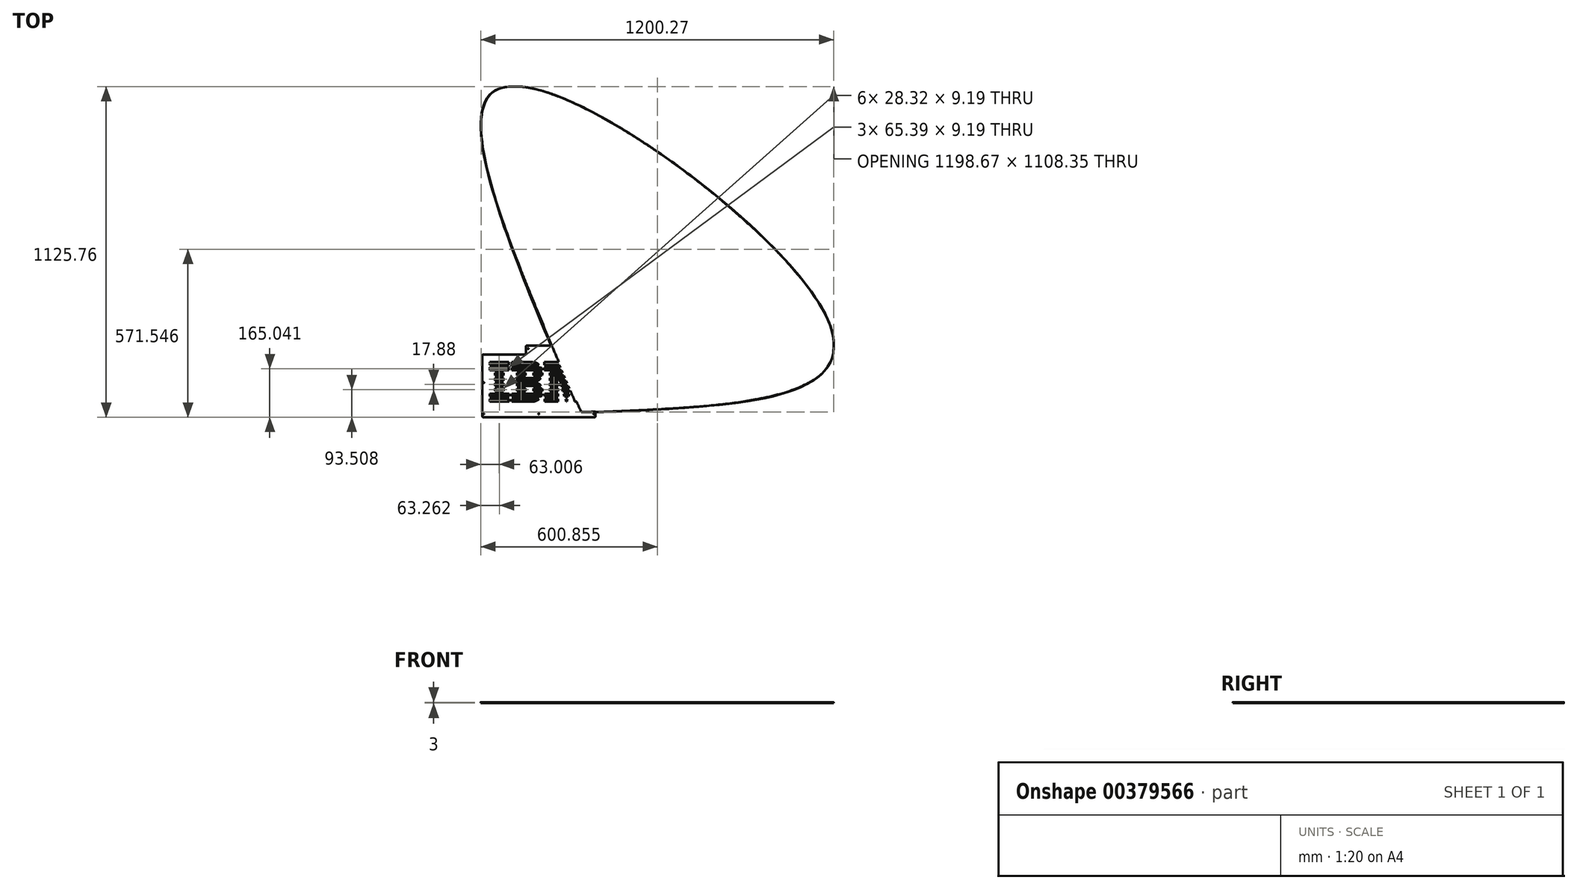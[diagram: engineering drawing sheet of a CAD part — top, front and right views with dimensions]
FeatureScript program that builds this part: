
annotation { "Feature Type Name" : "Feature", "Feature Type Description" : "" }
export const myFeature = defineFeature(function(context is Context, id is Id, definition is map)
    precondition{}
    {
        {
            var Q0;
            Q0=qCreatedBy(makeId("Top.planeOp"),FACE);
            var sketch = newSketch(context, id + "F0", { "sketchPlane" : qUnion([Q0])});
            skLineSegment(sketch, "E0.bottom", {"start": v(-188.4, -124.67) * mm, "end": v(188.48, -124.67) * mm});
            skLineSegment(sketch, "E0.left", {"start": v(-192.36, -120.71) * mm, "end": v(-192.36, 85.08) * mm});
            skPoint(sketch, "E1.visualSharp", {"position": v(-192.36, -124.67) * mm});
            skArc(sketch, "E1.filletArc", {"start": v(-192.36, -120.71) * mm, "mid": v(-191.2, -123.51) * mm, "end": v(-188.4, -124.67) * mm});
            skFitSpline(sketch, "E2", {"points": [v(151.72, -93.23) * mm, v(1000, 151.27) * mm, v(-92.62, 1000) * mm, v(150.35, -91.7) * mm]});
            skFitSpline(sketch, "E3", {"points": [v(147.19, -90.26) * mm, v(1000, 146.42) * mm, v(-90.07, 1000) * mm, v(145.01, -90.03) * mm]});
            skFitSpline(sketch, "E4", {"points": [v(149.93, -91.42) * mm, v(1000, 149.1) * mm, v(-90.88, 1000) * mm, v(148.23, -90.51) * mm]});
            skLineSegment(sketch, "E5", {"start": v(140.1, -108.72) * mm, "end": v(141.58, -106.96) * mm});
            skFitSpline(sketch, "E6", {"points": [v(139.4, -105.36) * mm, v(1000, 138.97) * mm, v(-106.35, 1000) * mm, v(138.57, -107.27) * mm]});
            skFitSpline(sketch, "E7", {"points": [v(141.58, -106.96) * mm, v(1000, 142.67) * mm, v(-105.67, 1000) * mm, v(143.1, -105.2) * mm]});
            skFitSpline(sketch, "E8", {"points": [v(144.18, -90.15) * mm, v(1000, 142.33) * mm, v(-90.45, 1000) * mm, v(140.47, -91.55) * mm]});
            skFitSpline(sketch, "E9", {"points": [v(144.37, -105.53) * mm, v(1000, 144.43) * mm, v(-105.53, 1000) * mm, v(144.48, -105.58) * mm]});
            skFitSpline(sketch, "E10", {"points": [v(144.87, -107.32) * mm, v(1000, 145.05) * mm, v(-108.17, 1000) * mm, v(145.23, -109) * mm]});
            skLineSegment(sketch, "E11", {"start": v(145.27, -109.17) * mm, "end": v(145.34, -109.48) * mm});
            skLineSegment(sketch, "E12", {"start": v(145.34, -109.48) * mm, "end": v(145.8, -109.46) * mm});
            skFitSpline(sketch, "E13", {"points": [v(139, -108.05) * mm, v(1000, 139.33) * mm, v(-108.27, 1000) * mm, v(139.7, -108.5) * mm]});
            skFitSpline(sketch, "E14", {"points": [v(145.8, -109.46) * mm, v(1000, 146.07) * mm, v(-109.46, 1000) * mm, v(146.5, -109.44) * mm]});
            skFitSpline(sketch, "E15", {"points": [v(139.4, -93) * mm, v(1000, 137.05) * mm, v(-96.17, 1000) * mm, v(137.32, -100.36) * mm]});
            skFitSpline(sketch, "E16", {"points": [v(140.2, -103.51) * mm, v(1000, 140.2) * mm, v(-103.54, 1000) * mm, v(139.83, -104.37) * mm]});
            skLineSegment(sketch, "E17", {"start": v(138.52, -107.41) * mm, "end": v(138.42, -107.66) * mm});
            skLineSegment(sketch, "E18", {"start": v(138.42, -107.66) * mm, "end": v(139, -108.05) * mm});
            skFitSpline(sketch, "E19", {"points": [v(143.16, -105.23) * mm, v(1000, 143.31) * mm, v(-105.29, 1000) * mm, v(144.27, -105.53) * mm]});
            skFitSpline(sketch, "E20", {"points": [v(144.5, -105.65) * mm, v(1000, 144.52) * mm, v(-105.72, 1000) * mm, v(144.68, -106.47) * mm]});
            skFitSpline(sketch, "E21", {"points": [v(140.05, -103.26) * mm, v(1000, 140.15) * mm, v(-103.37, 1000) * mm, v(140.22, -103.48) * mm]});
            skLineSegment(sketch, "E22", {"start": v(139.84, -108.58) * mm, "end": v(140.1, -108.72) * mm});
            skFitSpline(sketch, "E23", {"points": [v(147.38, -108.76) * mm, v(1000, 147.43) * mm, v(-108.06, 1000) * mm, v(147.64, -105.39) * mm]});
            skFitSpline(sketch, "E24", {"points": [v(146.8, -109.42) * mm, v(1000, 147.37) * mm, v(-109.38, 1000) * mm, v(147.33, -109.43) * mm]});
            skFitSpline(sketch, "E25", {"points": [v(149.02, -104.86) * mm, v(1000, 149.05) * mm, v(-104.86, 1000) * mm, v(149.6, -105.34) * mm]});
            skFitSpline(sketch, "E26", {"points": [v(147.65, -105.38) * mm, v(147.95, -105.27) * mm, v(148.3, -105.12) * mm]});
            skFitSpline(sketch, "E27", {"points": [v(148.3, -105.12) * mm, v(1000, 148.66) * mm, v(-104.98, 1000) * mm, v(148.98, -104.86) * mm]});
            skFitSpline(sketch, "E28", {"points": [v(150.24, -105.93) * mm, v(1000, 150.89) * mm, v(-106.5, 1000) * mm, v(151.63, -107.18) * mm]});
            skFitSpline(sketch, "E29", {"points": [v(151.89, -107.42) * mm, v(1000, 152.15) * mm, v(-107.65, 1000) * mm, v(152.4, -107.85) * mm]});
            skFitSpline(sketch, "E30", {"points": [v(152.44, -107.85) * mm, v(1000, 152.5) * mm, v(-107.85, 1000) * mm, v(153.4, -107.13) * mm]});
            skLineSegment(sketch, "E31", {"start": v(153.94, -106.64) * mm, "end": v(153.76, -106.32) * mm});
            skFitSpline(sketch, "E32", {"points": [v(153.76, -106.32) * mm, v(1000, 153.66) * mm, v(-106.14, 1000) * mm, v(153.14, -105.28) * mm]});
            skFitSpline(sketch, "E33", {"points": [v(152.62, -104.4) * mm, v(1000, 152.1) * mm, v(-103.53, 1000) * mm, v(151.66, -102.8) * mm]});
            skLineSegment(sketch, "E34", {"start": v(153.78, -106.8) * mm, "end": v(153.94, -106.64) * mm});
            skFitSpline(sketch, "E35", {"points": [v(151.66, -102.79) * mm, v(1000, 151.66) * mm, v(-102.77, 1000) * mm, v(151.8, -102.55) * mm]});
            skLineSegment(sketch, "E36", {"start": v(153.26, -98.4) * mm, "end": v(151.6, -98.41) * mm});
            skLineSegment(sketch, "E37", {"start": v(153.22, -98.72) * mm, "end": v(153.26, -98.4) * mm});
            skLineSegment(sketch, "E38", {"start": v(149.92, -98.43) * mm, "end": v(149.88, -98.78) * mm});
            skLineSegment(sketch, "E39", {"start": v(151.6, -98.41) * mm, "end": v(149.92, -98.43) * mm});
            skFitSpline(sketch, "E40", {"points": [v(149.88, -98.78) * mm, v(1000, 149.81) * mm, v(-99.41, 1000) * mm, v(149.5, -100.18) * mm]});
            skFitSpline(sketch, "E41", {"points": [v(149.07, -100.71) * mm, v(1000, 148.78) * mm, v(-101.08, 1000) * mm, v(148.06, -101.66) * mm]});
            skFitSpline(sketch, "E42", {"points": [v(151.96, -102.3) * mm, v(1000, 152.67) * mm, v(-101.24, 1000) * mm, v(153.1, -99.98) * mm]});
            skFitSpline(sketch, "E43", {"points": [v(142.86, -101.31) * mm, v(1000, 142.54) * mm, v(-101, 1000) * mm, v(142.5, -100.92) * mm]});
            skFitSpline(sketch, "E44", {"points": [v(145.1, -102.44) * mm, v(1000, 144.17) * mm, v(-102.32, 1000) * mm, v(143.57, -102.02) * mm]});
            skFitSpline(sketch, "E45", {"points": [v(144.2, -99.88) * mm, v(1000, 148.92) * mm, v(-97.14, 1000) * mm, v(152.68, -94.92) * mm]});
            skFitSpline(sketch, "E46", {"points": [v(142.56, -100.86) * mm, v(1000, 142.6) * mm, v(-100.82, 1000) * mm, v(143.34, -100.38) * mm]});
            skFitSpline(sketch, "E47", {"points": [v(152.7, -94.87) * mm, v(1000, 152.73) * mm, v(-94.79, 1000) * mm, v(152.12, -93.76) * mm]});
            skFitSpline(sketch, "E48", {"points": [v(147.58, -101.9) * mm, v(1000, 146.72) * mm, v(-102.35, 1000) * mm, v(145.85, -102.53) * mm]});
            skLineSegment(sketch, "E49", {"start": v(-44.4, 115.08) * mm, "end": v(-44.4, 111.04) * mm});
            skLineSegment(sketch, "E50.trimOffspring", {"start": v(-40.43, 119.04) * mm, "end": v(188.48, 119.04) * mm});
            skPoint(sketch, "E51.visualSharp", {"position": v(-44.4, 119.04) * mm});
            skArc(sketch, "E51.filletArc", {"start": v(-40.43, 119.04) * mm, "mid": v(-43.23, 117.88) * mm, "end": v(-44.4, 115.08) * mm});
            skLineSegment(sketch, "E52", {"start": v(192.44, 115.08) * mm, "end": v(192.44, -120.71) * mm});
            skPoint(sketch, "E53.visualSharp", {"position": v(192.44, 119.04) * mm});
            skArc(sketch, "E53.filletArc", {"start": v(192.44, 115.08) * mm, "mid": v(191.28, 117.88) * mm, "end": v(188.48, 119.04) * mm});
            skPoint(sketch, "E54.visualSharp", {"position": v(192.44, -124.67) * mm});
            skArc(sketch, "E54.filletArc", {"start": v(188.48, -124.67) * mm, "mid": v(191.28, -123.51) * mm, "end": v(192.44, -120.71) * mm});
            skLineSegment(sketch, "E55", {"start": v(-188.4, 89.04) * mm, "end": v(-44.4, 89.04) * mm});
            skLineSegment(sketch, "E56", {"start": v(-44.4, 89.04) * mm, "end": v(-44.4, 111.04) * mm});
            skPoint(sketch, "E57.visualSharp", {"position": v(-192.36, 89.04) * mm});
            skArc(sketch, "E57.filletArc", {"start": v(-188.4, 89.04) * mm, "mid": v(-191.2, 87.88) * mm, "end": v(-192.36, 85.08) * mm});
            skLineSegment(sketch, "E58", {"start": v(51.66, -17.88) * mm, "end": v(65.82, -17.88) * mm});
            skLineSegment(sketch, "E59", {"start": v(65.82, -17.88) * mm, "end": v(65.82, -13.28) * mm});
            skLineSegment(sketch, "E60", {"start": v(65.82, -8.68) * mm, "end": v(51.66, -8.68) * mm});
            skLineSegment(sketch, "E61", {"start": v(51.66, -8.68) * mm, "end": v(37.5, -8.68) * mm});
            skLineSegment(sketch, "E62", {"start": v(121.42, 2.56) * mm, "end": v(121.42, 0) * mm});
            skLineSegment(sketch, "E63", {"start": v(121.42, 0) * mm, "end": v(135.58, 0) * mm});
            skLineSegment(sketch, "E64", {"start": v(37.5, -13.28) * mm, "end": v(37.5, -17.88) * mm});
            skLineSegment(sketch, "E65", {"start": v(135.58, 0) * mm, "end": v(149.74, 0) * mm});
            skLineSegment(sketch, "E66", {"start": v(37.5, -17.88) * mm, "end": v(51.66, -17.88) * mm});
            skLineSegment(sketch, "E67", {"start": v(149.74, 4.6) * mm, "end": v(149.74, 9.2) * mm});
            skLineSegment(sketch, "E68", {"start": v(149.74, 9.2) * mm, "end": v(123.16, 9.2) * mm});
            skLineSegment(sketch, "E69", {"start": v(121.42, 5.12) * mm, "end": v(121.42, 2.56) * mm});
            skLineSegment(sketch, "E70", {"start": v(123.16, 9.2) * mm, "end": v(96.58, 9.2) * mm});
            skLineSegment(sketch, "E71", {"start": v(149.74, 0) * mm, "end": v(149.74, 4.6) * mm});
            skLineSegment(sketch, "E72", {"start": v(37.5, -8.68) * mm, "end": v(37.5, -13.28) * mm});
            skLineSegment(sketch, "E73", {"start": v(65.82, -13.28) * mm, "end": v(65.82, -8.68) * mm});
            skLineSegment(sketch, "E74", {"start": v(3.4, 4.66) * mm, "end": v(1.14, 2.34) * mm});
            skLineSegment(sketch, "E75", {"start": v(37.5, 4.6) * mm, "end": v(37.5, 0) * mm});
            skLineSegment(sketch, "E76", {"start": v(8.17, -53.35) * mm, "end": v(8.91, -52.29) * mm});
            skLineSegment(sketch, "E77", {"start": v(-1.63, 0) * mm, "end": v(-37.8, 0) * mm});
            skLineSegment(sketch, "E78", {"start": v(-73.96, 4.6) * mm, "end": v(-73.96, 9.2) * mm});
            skLineSegment(sketch, "E79", {"start": v(-92.75, -49.05) * mm, "end": v(-92.75, -53.65) * mm});
            skLineSegment(sketch, "E80", {"start": v(10.22, 17.88) * mm, "end": v(11.57, 22.61) * mm});
            skLineSegment(sketch, "E81", {"start": v(-73.96, 9.2) * mm, "end": v(-33.8, 9.2) * mm});
            skLineSegment(sketch, "E82", {"start": v(90.93, 9.2) * mm, "end": v(64.22, 9.2) * mm});
            skLineSegment(sketch, "E83", {"start": v(-18.1, -26.56) * mm, "end": v(-18.1, -31.16) * mm});
            skLineSegment(sketch, "E84", {"start": v(-33.8, 9.2) * mm, "end": v(6.35, 9.2) * mm});
            skLineSegment(sketch, "E85", {"start": v(64.22, 9.2) * mm, "end": v(37.5, 9.2) * mm});
            skLineSegment(sketch, "E86", {"start": v(-42.42, -53.65) * mm, "end": v(7.91, -53.65) * mm});
            skLineSegment(sketch, "E87", {"start": v(65.82, 5.12) * mm, "end": v(66.72, 2.56) * mm});
            skLineSegment(sketch, "E88", {"start": v(168.54, -66.93) * mm, "end": v(168.54, -71.53) * mm});
            skLineSegment(sketch, "E89", {"start": v(37.5, 9.2) * mm, "end": v(37.5, 4.6) * mm});
            skLineSegment(sketch, "E90", {"start": v(121.42, -66.93) * mm, "end": v(121.42, -62.34) * mm});
            skLineSegment(sketch, "E91", {"start": v(93.56, 0) * mm, "end": v(119.5, 0) * mm});
            skLineSegment(sketch, "E92", {"start": v(-92.75, -53.65) * mm, "end": v(-42.42, -53.65) * mm});
            skLineSegment(sketch, "E93", {"start": v(8.91, -52.29) * mm, "end": v(9.8, -50.3) * mm});
            skLineSegment(sketch, "E94", {"start": v(-40.75, -44.44) * mm, "end": v(-92.75, -44.44) * mm});
            skLineSegment(sketch, "E95", {"start": v(-3.94, 17.88) * mm, "end": v(10.22, 17.88) * mm});
            skLineSegment(sketch, "E96", {"start": v(119.5, 0) * mm, "end": v(120.46, 2.56) * mm});
            skLineSegment(sketch, "E97", {"start": v(11.57, -31.3) * mm, "end": v(10.22, -26.56) * mm});
            skLineSegment(sketch, "E98", {"start": v(92.34, 5.3) * mm, "end": v(90.93, 9.2) * mm});
            skLineSegment(sketch, "E99", {"start": v(96.58, 9.2) * mm, "end": v(95.17, 5.3) * mm});
            skLineSegment(sketch, "E100", {"start": v(-3.94, -26.56) * mm, "end": v(-18.1, -26.56) * mm});
            skLineSegment(sketch, "E101", {"start": v(-18.1, -35.76) * mm, "end": v(-3.04, -35.76) * mm});
            skLineSegment(sketch, "E102", {"start": v(-3.04, -35.76) * mm, "end": v(12.02, -35.76) * mm});
            skLineSegment(sketch, "E103", {"start": v(12.02, -35.76) * mm, "end": v(11.9, -33.56) * mm});
            skLineSegment(sketch, "E104", {"start": v(10.22, -26.56) * mm, "end": v(-3.94, -26.56) * mm});
            skLineSegment(sketch, "E105", {"start": v(65.82, 2.56) * mm, "end": v(65.82, 5.12) * mm});
            skLineSegment(sketch, "E106", {"start": v(121.42, -71.53) * mm, "end": v(121.42, -66.93) * mm});
            skLineSegment(sketch, "E107", {"start": v(121.42, -62.34) * mm, "end": v(144.98, -62.34) * mm});
            skLineSegment(sketch, "E108", {"start": v(144.98, -62.34) * mm, "end": v(168.54, -62.34) * mm});
            skLineSegment(sketch, "E109", {"start": v(95.17, 5.3) * mm, "end": v(93.76, 1.4) * mm});
            skLineSegment(sketch, "E110", {"start": v(168.54, -62.34) * mm, "end": v(168.54, -66.93) * mm});
            skLineSegment(sketch, "E111", {"start": v(168.54, -71.53) * mm, "end": v(144.98, -71.53) * mm});
            skLineSegment(sketch, "E112", {"start": v(144.98, -71.53) * mm, "end": v(121.42, -71.53) * mm});
            skLineSegment(sketch, "E113", {"start": v(-18.1, 17.88) * mm, "end": v(-3.94, 17.88) * mm});
            skLineSegment(sketch, "E114", {"start": v(11.9, -33.56) * mm, "end": v(11.57, -31.3) * mm});
            skLineSegment(sketch, "E115", {"start": v(5.13, 6.94) * mm, "end": v(3.4, 4.66) * mm});
            skLineSegment(sketch, "E116", {"start": v(1.14, 2.34) * mm, "end": v(-1.63, 0) * mm});
            skLineSegment(sketch, "E117", {"start": v(-18.1, 22.48) * mm, "end": v(-18.1, 17.88) * mm});
            skLineSegment(sketch, "E118", {"start": v(-3.04, 27.09) * mm, "end": v(-18.1, 27.09) * mm});
            skLineSegment(sketch, "E119", {"start": v(-37.8, 0) * mm, "end": v(-73.96, 0) * mm});
            skLineSegment(sketch, "E120", {"start": v(-73.96, 0) * mm, "end": v(-73.96, 4.6) * mm});
            skLineSegment(sketch, "E121", {"start": v(11.25, -44.44) * mm, "end": v(-40.75, -44.44) * mm});
            skLineSegment(sketch, "E122", {"start": v(10.58, -47.68) * mm, "end": v(11.25, -44.44) * mm});
            skLineSegment(sketch, "E123", {"start": v(66.72, 2.56) * mm, "end": v(67.62, 0) * mm});
            skLineSegment(sketch, "E124", {"start": v(51.66, 0) * mm, "end": v(65.82, 0) * mm});
            skLineSegment(sketch, "E125", {"start": v(-92.75, -44.44) * mm, "end": v(-92.75, -49.05) * mm});
            skLineSegment(sketch, "E126", {"start": v(11.57, 22.61) * mm, "end": v(11.9, 24.88) * mm});
            skLineSegment(sketch, "E127", {"start": v(-18.1, -31.16) * mm, "end": v(-18.1, -35.76) * mm});
            skLineSegment(sketch, "E128", {"start": v(67.62, 0) * mm, "end": v(93.56, 0) * mm});
            skLineSegment(sketch, "E129", {"start": v(7.91, -53.65) * mm, "end": v(8.17, -53.35) * mm});
            skLineSegment(sketch, "E130", {"start": v(-18.1, 27.09) * mm, "end": v(-18.1, 22.48) * mm});
            skLineSegment(sketch, "E131", {"start": v(65.82, 0) * mm, "end": v(65.82, 2.56) * mm});
            skLineSegment(sketch, "E132", {"start": v(9.8, -50.3) * mm, "end": v(10.58, -47.68) * mm});
            skLineSegment(sketch, "E133", {"start": v(37.5, 0) * mm, "end": v(51.66, 0) * mm});
            skLineSegment(sketch, "E134", {"start": v(120.46, 2.56) * mm, "end": v(121.42, 5.12) * mm});
            skLineSegment(sketch, "E135", {"start": v(11.9, 24.88) * mm, "end": v(12.02, 27.09) * mm});
            skLineSegment(sketch, "E136", {"start": v(12.02, 27.09) * mm, "end": v(-3.04, 27.09) * mm});
            skLineSegment(sketch, "E137", {"start": v(93.76, 1.4) * mm, "end": v(92.34, 5.3) * mm});
            skLineSegment(sketch, "E138", {"start": v(114.92, -13.28) * mm, "end": v(113.29, -17.88) * mm});
            skLineSegment(sketch, "E139", {"start": v(93.76, -35.76) * mm, "end": v(80.72, -35.76) * mm});
            skLineSegment(sketch, "E140", {"start": v(65.82, -66.93) * mm, "end": v(65.82, -62.34) * mm});
            skLineSegment(sketch, "E141", {"start": v(80.72, -35.76) * mm, "end": v(79.06, -31.16) * mm});
            skLineSegment(sketch, "E142", {"start": v(37.5, 17.88) * mm, "end": v(37.5, 22.48) * mm});
            skLineSegment(sketch, "E143", {"start": v(-33.8, -17.88) * mm, "end": v(-73.96, -17.88) * mm});
            skLineSegment(sketch, "E144", {"start": v(65.82, -62.34) * mm, "end": v(42.52, -62.34) * mm});
            skLineSegment(sketch, "E145", {"start": v(-2, 55.8) * mm, "end": v(-4.52, 57.68) * mm});
            skLineSegment(sketch, "E146", {"start": v(93.76, -8.68) * mm, "end": v(116.54, -8.68) * mm});
            skLineSegment(sketch, "E147", {"start": v(3.4, -13.35) * mm, "end": v(5.13, -15.63) * mm});
            skLineSegment(sketch, "E148", {"start": v(-92.75, 62.85) * mm, "end": v(-92.75, 58.25) * mm});
            skLineSegment(sketch, "E149", {"start": v(1.14, -11.03) * mm, "end": v(3.4, -13.35) * mm});
            skLineSegment(sketch, "E150", {"start": v(113.29, -17.88) * mm, "end": v(93.84, -17.88) * mm});
            skLineSegment(sketch, "E151", {"start": v(70.97, -8.68) * mm, "end": v(93.76, -8.68) * mm});
            skLineSegment(sketch, "E152", {"start": v(0.43, 53.65) * mm, "end": v(-2, 55.8) * mm});
            skLineSegment(sketch, "E153", {"start": v(-15.58, 62.27) * mm, "end": v(-18.59, 62.7) * mm});
            skLineSegment(sketch, "E154", {"start": v(72.68, -13.28) * mm, "end": v(70.97, -8.68) * mm});
            skLineSegment(sketch, "E155", {"start": v(19.22, -66.93) * mm, "end": v(19.22, -71.53) * mm});
            skLineSegment(sketch, "E156", {"start": v(5.13, -15.63) * mm, "end": v(6.35, -17.88) * mm});
            skLineSegment(sketch, "E157", {"start": v(-73.96, -26.56) * mm, "end": v(-73.96, -31.16) * mm});
            skLineSegment(sketch, "E158", {"start": v(-4.52, 57.68) * mm, "end": v(-7.14, 59.26) * mm});
            skLineSegment(sketch, "E159", {"start": v(-73.96, -31.16) * mm, "end": v(-73.96, -35.76) * mm});
            skLineSegment(sketch, "E160", {"start": v(-12.67, 61.55) * mm, "end": v(-15.58, 62.27) * mm});
            skLineSegment(sketch, "E161", {"start": v(-45.64, -35.76) * mm, "end": v(-45.64, -31.16) * mm});
            skLineSegment(sketch, "E162", {"start": v(74.4, -17.88) * mm, "end": v(72.68, -13.28) * mm});
            skLineSegment(sketch, "E163", {"start": v(-73.96, -17.88) * mm, "end": v(-73.96, -13.28) * mm});
            skLineSegment(sketch, "E164", {"start": v(19.22, -62.34) * mm, "end": v(19.22, -66.93) * mm});
            skLineSegment(sketch, "E165", {"start": v(-57.22, 62.85) * mm, "end": v(-92.75, 62.85) * mm});
            skLineSegment(sketch, "E166", {"start": v(-73.96, -8.68) * mm, "end": v(-37.8, -8.68) * mm});
            skLineSegment(sketch, "E167", {"start": v(84.37, 27.09) * mm, "end": v(86.04, 22.48) * mm});
            skLineSegment(sketch, "E168", {"start": v(87.71, 17.88) * mm, "end": v(62.6, 17.88) * mm});
            skLineSegment(sketch, "E169", {"start": v(-92.75, 58.25) * mm, "end": v(-92.75, 53.65) * mm});
            skLineSegment(sketch, "E170", {"start": v(6.35, 9.2) * mm, "end": v(5.13, 6.94) * mm});
            skLineSegment(sketch, "E171", {"start": v(60.93, 27.09) * mm, "end": v(84.37, 27.09) * mm});
            skLineSegment(sketch, "E172", {"start": v(37.5, 22.48) * mm, "end": v(37.5, 27.09) * mm});
            skLineSegment(sketch, "E173", {"start": v(37.5, 27.09) * mm, "end": v(60.93, 27.09) * mm});
            skLineSegment(sketch, "E174", {"start": v(-73.96, -13.28) * mm, "end": v(-73.96, -8.68) * mm});
            skLineSegment(sketch, "E175", {"start": v(93.84, -17.88) * mm, "end": v(74.4, -17.88) * mm});
            skLineSegment(sketch, "E176", {"start": v(42.52, -71.53) * mm, "end": v(65.82, -71.53) * mm});
            skLineSegment(sketch, "E177", {"start": v(62.6, 17.88) * mm, "end": v(37.5, 17.88) * mm});
            skLineSegment(sketch, "E178", {"start": v(-18.59, 62.7) * mm, "end": v(-21.7, 62.85) * mm});
            skLineSegment(sketch, "E179", {"start": v(116.54, -8.68) * mm, "end": v(114.92, -13.28) * mm});
            skLineSegment(sketch, "E180", {"start": v(19.22, -71.53) * mm, "end": v(42.52, -71.53) * mm});
            skLineSegment(sketch, "E181", {"start": v(-1.63, -8.68) * mm, "end": v(1.14, -11.03) * mm});
            skLineSegment(sketch, "E182", {"start": v(-21.7, 62.85) * mm, "end": v(-57.22, 62.85) * mm});
            skLineSegment(sketch, "E183", {"start": v(-92.75, 53.65) * mm, "end": v(-46.16, 53.65) * mm});
            skLineSegment(sketch, "E184", {"start": v(-46.16, 53.65) * mm, "end": v(0.43, 53.65) * mm});
            skLineSegment(sketch, "E185", {"start": v(-37.8, -8.68) * mm, "end": v(-1.63, -8.68) * mm});
            skLineSegment(sketch, "E186", {"start": v(-7.14, 59.26) * mm, "end": v(-9.86, 60.55) * mm});
            skLineSegment(sketch, "E187", {"start": v(-9.86, 60.55) * mm, "end": v(-12.67, 61.55) * mm});
            skLineSegment(sketch, "E188", {"start": v(-59.8, -26.56) * mm, "end": v(-73.96, -26.56) * mm});
            skLineSegment(sketch, "E189", {"start": v(-73.96, -35.76) * mm, "end": v(-59.8, -35.76) * mm});
            skLineSegment(sketch, "E190", {"start": v(86.04, 22.48) * mm, "end": v(87.71, 17.88) * mm});
            skLineSegment(sketch, "E191", {"start": v(-59.8, -35.76) * mm, "end": v(-45.64, -35.76) * mm});
            skLineSegment(sketch, "E192", {"start": v(77.4, -26.56) * mm, "end": v(93.77, -26.56) * mm});
            skLineSegment(sketch, "E193", {"start": v(42.52, -62.34) * mm, "end": v(19.22, -62.34) * mm});
            skLineSegment(sketch, "E194", {"start": v(-45.64, -26.56) * mm, "end": v(-59.8, -26.56) * mm});
            skLineSegment(sketch, "E195", {"start": v(65.82, -71.53) * mm, "end": v(65.82, -66.93) * mm});
            skLineSegment(sketch, "E196", {"start": v(110.14, -26.56) * mm, "end": v(108.47, -31.16) * mm});
            skLineSegment(sketch, "E197", {"start": v(-45.64, -31.16) * mm, "end": v(-45.64, -26.56) * mm});
            skLineSegment(sketch, "E198", {"start": v(6.35, -17.88) * mm, "end": v(-33.8, -17.88) * mm});
            skLineSegment(sketch, "E199", {"start": v(108.47, -31.16) * mm, "end": v(106.8, -35.76) * mm});
            skLineSegment(sketch, "E200", {"start": v(106.8, -35.76) * mm, "end": v(93.76, -35.76) * mm});
            skLineSegment(sketch, "E201", {"start": v(93.77, -26.56) * mm, "end": v(110.14, -26.56) * mm});
            skLineSegment(sketch, "E202", {"start": v(79.06, -31.16) * mm, "end": v(77.4, -26.56) * mm});
            skLineSegment(sketch, "E203", {"start": v(-45.64, 27.09) * mm, "end": v(-45.64, 22.48) * mm});
            skLineSegment(sketch, "E204", {"start": v(-45.64, 17.88) * mm, "end": v(-59.8, 17.88) * mm});
            skLineSegment(sketch, "E205", {"start": v(-59.8, 17.88) * mm, "end": v(-73.96, 17.88) * mm});
            skLineSegment(sketch, "E206", {"start": v(93.87, -71.51) * mm, "end": v(94.16, -71.52) * mm});
            skLineSegment(sketch, "E207", {"start": v(-120.3, 0) * mm, "end": v(-120.3, 4.6) * mm});
            skLineSegment(sketch, "E208", {"start": v(83.84, -44.44) * mm, "end": v(85.55, -49.05) * mm});
            skLineSegment(sketch, "E209", {"start": v(75.09, 53.65) * mm, "end": v(73.41, 58.25) * mm});
            skLineSegment(sketch, "E210", {"start": v(0.43, -62.34) * mm, "end": v(-2, -64.49) * mm});
            skLineSegment(sketch, "E211", {"start": v(-148.62, 0) * mm, "end": v(-134.46, 0) * mm});
            skLineSegment(sketch, "E212", {"start": v(-15.58, -70.94) * mm, "end": v(-18.59, -71.37) * mm});
            skLineSegment(sketch, "E213", {"start": v(103.72, -44.44) * mm, "end": v(93.78, -44.44) * mm});
            skLineSegment(sketch, "E214", {"start": v(19.22, -44.44) * mm, "end": v(42.52, -44.44) * mm});
            skLineSegment(sketch, "E215", {"start": v(73.41, 58.25) * mm, "end": v(71.74, 62.85) * mm});
            skLineSegment(sketch, "E216", {"start": v(18.71, 62.85) * mm, "end": v(18.71, 58.25) * mm});
            skLineSegment(sketch, "E217", {"start": v(42.52, -44.44) * mm, "end": v(65.82, -44.44) * mm});
            skLineSegment(sketch, "E218", {"start": v(-45.64, 22.48) * mm, "end": v(-45.64, 17.88) * mm});
            skLineSegment(sketch, "E219", {"start": v(-73.96, 17.88) * mm, "end": v(-73.96, 22.48) * mm});
            skLineSegment(sketch, "E220", {"start": v(-18.59, -71.37) * mm, "end": v(-21.7, -71.52) * mm});
            skLineSegment(sketch, "E221", {"start": v(-7.14, -67.93) * mm, "end": v(-9.86, -69.22) * mm});
            skLineSegment(sketch, "E222", {"start": v(-134.46, -8.68) * mm, "end": v(-148.62, -8.68) * mm});
            skLineSegment(sketch, "E223", {"start": v(-73.96, 22.48) * mm, "end": v(-73.96, 27.09) * mm});
            skLineSegment(sketch, "E224", {"start": v(-12.67, -70.23) * mm, "end": v(-15.58, -70.94) * mm});
            skLineSegment(sketch, "E225", {"start": v(18.71, 53.65) * mm, "end": v(46.9, 53.65) * mm});
            skLineSegment(sketch, "E226", {"start": v(-92.75, -66.93) * mm, "end": v(-92.75, -62.34) * mm});
            skLineSegment(sketch, "E227", {"start": v(71.74, 62.85) * mm, "end": v(45.23, 62.85) * mm});
            skLineSegment(sketch, "E228", {"start": v(-92.75, -71.52) * mm, "end": v(-92.75, -66.93) * mm});
            skLineSegment(sketch, "E229", {"start": v(-2, -64.49) * mm, "end": v(-4.52, -66.35) * mm});
            skLineSegment(sketch, "E230", {"start": v(93.78, -44.44) * mm, "end": v(83.84, -44.44) * mm});
            skLineSegment(sketch, "E231", {"start": v(45.23, 62.85) * mm, "end": v(18.71, 62.85) * mm});
            skLineSegment(sketch, "E232", {"start": v(65.82, -49.05) * mm, "end": v(65.82, -53.65) * mm});
            skLineSegment(sketch, "E233", {"start": v(-120.3, -17.88) * mm, "end": v(-120.3, -13.28) * mm});
            skLineSegment(sketch, "E234", {"start": v(-120.3, -13.28) * mm, "end": v(-120.3, -8.68) * mm});
            skLineSegment(sketch, "E235", {"start": v(-59.8, 27.09) * mm, "end": v(-45.64, 27.09) * mm});
            skLineSegment(sketch, "E236", {"start": v(-9.86, -69.22) * mm, "end": v(-12.67, -70.23) * mm});
            skLineSegment(sketch, "E237", {"start": v(-46.16, -62.34) * mm, "end": v(0.43, -62.34) * mm});
            skLineSegment(sketch, "E238", {"start": v(100.52, -53.65) * mm, "end": v(102.12, -49.05) * mm});
            skLineSegment(sketch, "E239", {"start": v(19.22, -53.65) * mm, "end": v(19.22, -49.05) * mm});
            skLineSegment(sketch, "E240", {"start": v(-134.46, 0) * mm, "end": v(-120.3, 0) * mm});
            skLineSegment(sketch, "E241", {"start": v(102.12, -49.05) * mm, "end": v(103.72, -44.44) * mm});
            skLineSegment(sketch, "E242", {"start": v(-148.62, 9.2) * mm, "end": v(-148.62, 4.6) * mm});
            skLineSegment(sketch, "E243", {"start": v(85.55, -49.05) * mm, "end": v(87.25, -53.65) * mm});
            skLineSegment(sketch, "E244", {"start": v(-148.62, 4.6) * mm, "end": v(-148.62, 0) * mm});
            skLineSegment(sketch, "E245", {"start": v(18.71, 58.25) * mm, "end": v(18.71, 53.65) * mm});
            skLineSegment(sketch, "E246", {"start": v(-21.7, -71.52) * mm, "end": v(-57.22, -71.52) * mm});
            skLineSegment(sketch, "E247", {"start": v(-57.22, -71.52) * mm, "end": v(-92.75, -71.52) * mm});
            skLineSegment(sketch, "E248", {"start": v(87.25, -53.65) * mm, "end": v(93.89, -53.65) * mm});
            skLineSegment(sketch, "E249", {"start": v(-92.75, -62.34) * mm, "end": v(-46.16, -62.34) * mm});
            skLineSegment(sketch, "E250", {"start": v(19.22, -49.05) * mm, "end": v(19.22, -44.44) * mm});
            skLineSegment(sketch, "E251", {"start": v(42.52, -53.65) * mm, "end": v(19.22, -53.65) * mm});
            skLineSegment(sketch, "E252", {"start": v(-134.46, -17.88) * mm, "end": v(-120.3, -17.88) * mm});
            skLineSegment(sketch, "E253", {"start": v(-120.3, -8.68) * mm, "end": v(-134.46, -8.68) * mm});
            skLineSegment(sketch, "E254", {"start": v(-148.62, -13.28) * mm, "end": v(-148.62, -17.88) * mm});
            skLineSegment(sketch, "E255", {"start": v(-120.3, 4.6) * mm, "end": v(-120.3, 9.2) * mm});
            skLineSegment(sketch, "E256", {"start": v(-148.62, -17.88) * mm, "end": v(-134.46, -17.88) * mm});
            skLineSegment(sketch, "E257", {"start": v(-73.96, 27.09) * mm, "end": v(-59.8, 27.09) * mm});
            skLineSegment(sketch, "E258", {"start": v(-4.52, -66.35) * mm, "end": v(-7.14, -67.93) * mm});
            skLineSegment(sketch, "E259", {"start": v(-120.3, 9.2) * mm, "end": v(-134.46, 9.2) * mm});
            skLineSegment(sketch, "E260", {"start": v(-134.46, 9.2) * mm, "end": v(-148.62, 9.2) * mm});
            skLineSegment(sketch, "E261", {"start": v(93.89, -53.65) * mm, "end": v(100.52, -53.65) * mm});
            skLineSegment(sketch, "E262", {"start": v(46.9, 53.65) * mm, "end": v(75.09, 53.65) * mm});
            skLineSegment(sketch, "E263", {"start": v(65.82, -44.44) * mm, "end": v(65.82, -49.05) * mm});
            skLineSegment(sketch, "E264", {"start": v(65.82, -53.65) * mm, "end": v(42.52, -53.65) * mm});
            skLineSegment(sketch, "E265", {"start": v(-148.62, -8.68) * mm, "end": v(-148.62, -13.28) * mm});
            skLineSegment(sketch, "E266", {"start": v(-102.02, 58.25) * mm, "end": v(-102.02, 53.65) * mm});
            skLineSegment(sketch, "E267", {"start": v(-134.46, 27.09) * mm, "end": v(-148.62, 27.09) * mm});
            skLineSegment(sketch, "E268", {"start": v(-134.46, 17.88) * mm, "end": v(-120.3, 17.88) * mm});
            skLineSegment(sketch, "E269", {"start": v(-92.75, 35.77) * mm, "end": v(-40.75, 35.77) * mm});
            skLineSegment(sketch, "E270", {"start": v(-102.02, 53.65) * mm, "end": v(-134.71, 53.65) * mm});
            skLineSegment(sketch, "E271", {"start": v(97.49, -62.34) * mm, "end": v(93.9, -62.34) * mm});
            skLineSegment(sketch, "E272", {"start": v(78.17, 44.95) * mm, "end": v(48.44, 44.95) * mm});
            skLineSegment(sketch, "E273", {"start": v(-134.71, 53.65) * mm, "end": v(-167.4, 53.65) * mm});
            skLineSegment(sketch, "E274", {"start": v(-167.4, 58.25) * mm, "end": v(-167.4, 62.85) * mm});
            skLineSegment(sketch, "E275", {"start": v(102.65, 27.09) * mm, "end": v(126.2, 27.09) * mm});
            skLineSegment(sketch, "E276", {"start": v(48.44, 44.95) * mm, "end": v(18.71, 44.95) * mm});
            skLineSegment(sketch, "E277", {"start": v(149.74, -13.28) * mm, "end": v(149.74, -17.88) * mm});
            skLineSegment(sketch, "E278", {"start": v(7.91, 44.95) * mm, "end": v(-42.42, 44.95) * mm});
            skLineSegment(sketch, "E279", {"start": v(135.58, -17.88) * mm, "end": v(121.42, -17.88) * mm});
            skLineSegment(sketch, "E280", {"start": v(-148.62, 27.09) * mm, "end": v(-148.62, 22.48) * mm});
            skLineSegment(sketch, "E281", {"start": v(126.2, 27.09) * mm, "end": v(149.74, 27.09) * mm});
            skLineSegment(sketch, "E282", {"start": v(91.95, -66.92) * mm, "end": v(93.6, -71.5) * mm});
            skLineSegment(sketch, "E283", {"start": v(18.71, 44.95) * mm, "end": v(18.71, 40.36) * mm});
            skLineSegment(sketch, "E284", {"start": v(50, 35.77) * mm, "end": v(81.27, 35.77) * mm});
            skLineSegment(sketch, "E285", {"start": v(-148.62, 22.48) * mm, "end": v(-148.62, 17.88) * mm});
            skLineSegment(sketch, "E286", {"start": v(149.74, -17.88) * mm, "end": v(135.58, -17.88) * mm});
            skLineSegment(sketch, "E287", {"start": v(-40.75, 35.77) * mm, "end": v(11.25, 35.77) * mm});
            skLineSegment(sketch, "E288", {"start": v(9.8, 41.6) * mm, "end": v(8.91, 43.6) * mm});
            skLineSegment(sketch, "E289", {"start": v(-167.4, 62.85) * mm, "end": v(-134.71, 62.85) * mm});
            skLineSegment(sketch, "E290", {"start": v(93.6, -71.5) * mm, "end": v(93.87, -71.51) * mm});
            skLineSegment(sketch, "E291", {"start": v(-120.3, 17.88) * mm, "end": v(-120.3, 22.48) * mm});
            skLineSegment(sketch, "E292", {"start": v(149.74, 17.88) * mm, "end": v(124.52, 17.88) * mm});
            skLineSegment(sketch, "E293", {"start": v(79.72, 40.36) * mm, "end": v(78.17, 44.95) * mm});
            skLineSegment(sketch, "E294", {"start": v(121.42, -13.28) * mm, "end": v(121.42, -8.68) * mm});
            skLineSegment(sketch, "E295", {"start": v(8.91, 43.6) * mm, "end": v(8.17, 44.65) * mm});
            skLineSegment(sketch, "E296", {"start": v(18.71, 40.36) * mm, "end": v(18.71, 35.77) * mm});
            skLineSegment(sketch, "E297", {"start": v(-92.75, 40.36) * mm, "end": v(-92.75, 35.77) * mm});
            skLineSegment(sketch, "E298", {"start": v(-167.4, 53.65) * mm, "end": v(-167.4, 58.25) * mm});
            skLineSegment(sketch, "E299", {"start": v(115.5, 62.85) * mm, "end": v(141.77, 62.85) * mm});
            skLineSegment(sketch, "E300", {"start": v(8.17, 44.65) * mm, "end": v(7.91, 44.95) * mm});
            skLineSegment(sketch, "E301", {"start": v(-42.42, 44.95) * mm, "end": v(-92.75, 44.95) * mm});
            skLineSegment(sketch, "E302", {"start": v(141.77, 62.85) * mm, "end": v(168.02, 62.85) * mm});
            skLineSegment(sketch, "E303", {"start": v(168.02, 62.85) * mm, "end": v(168.02, 58.25) * mm});
            skLineSegment(sketch, "E304", {"start": v(168.02, 58.25) * mm, "end": v(168.02, 53.65) * mm});
            skLineSegment(sketch, "E305", {"start": v(168.02, 53.65) * mm, "end": v(140.1, 53.65) * mm});
            skLineSegment(sketch, "E306", {"start": v(140.1, 53.65) * mm, "end": v(112.16, 53.65) * mm});
            skLineSegment(sketch, "E307", {"start": v(99.29, 17.88) * mm, "end": v(100.97, 22.48) * mm});
            skLineSegment(sketch, "E308", {"start": v(90.31, -62.34) * mm, "end": v(91.95, -66.92) * mm});
            skLineSegment(sketch, "E309", {"start": v(-120.3, 22.48) * mm, "end": v(-120.3, 27.09) * mm});
            skLineSegment(sketch, "E310", {"start": v(149.74, 27.09) * mm, "end": v(149.74, 22.48) * mm});
            skLineSegment(sketch, "E311", {"start": v(-120.3, 27.09) * mm, "end": v(-134.46, 27.09) * mm});
            skLineSegment(sketch, "E312", {"start": v(18.71, 35.77) * mm, "end": v(50, 35.77) * mm});
            skLineSegment(sketch, "E313", {"start": v(135.58, -8.68) * mm, "end": v(149.74, -8.68) * mm});
            skLineSegment(sketch, "E314", {"start": v(121.42, -17.88) * mm, "end": v(121.42, -13.28) * mm});
            skLineSegment(sketch, "E315", {"start": v(-92.75, 44.95) * mm, "end": v(-92.75, 40.36) * mm});
            skLineSegment(sketch, "E316", {"start": v(94.16, -71.52) * mm, "end": v(95.82, -66.93) * mm});
            skLineSegment(sketch, "E317", {"start": v(93.9, -62.34) * mm, "end": v(90.31, -62.34) * mm});
            skLineSegment(sketch, "E318", {"start": v(100.97, 22.48) * mm, "end": v(102.65, 27.09) * mm});
            skLineSegment(sketch, "E319", {"start": v(121.42, -8.68) * mm, "end": v(135.58, -8.68) * mm});
            skLineSegment(sketch, "E320", {"start": v(-148.62, 17.88) * mm, "end": v(-134.46, 17.88) * mm});
            skLineSegment(sketch, "E321", {"start": v(149.74, -8.68) * mm, "end": v(149.74, -13.28) * mm});
            skLineSegment(sketch, "E322", {"start": v(149.74, 22.48) * mm, "end": v(149.74, 17.88) * mm});
            skLineSegment(sketch, "E323", {"start": v(11.25, 35.77) * mm, "end": v(10.58, 39) * mm});
            skLineSegment(sketch, "E324", {"start": v(10.58, 39) * mm, "end": v(9.8, 41.6) * mm});
            skLineSegment(sketch, "E325", {"start": v(124.52, 17.88) * mm, "end": v(99.29, 17.88) * mm});
            skLineSegment(sketch, "E326", {"start": v(-134.71, 62.85) * mm, "end": v(-102.02, 62.85) * mm});
            skLineSegment(sketch, "E327", {"start": v(95.82, -66.93) * mm, "end": v(97.49, -62.34) * mm});
            skLineSegment(sketch, "E328", {"start": v(81.27, 35.77) * mm, "end": v(79.72, 40.36) * mm});
            skLineSegment(sketch, "E329", {"start": v(-102.02, 62.85) * mm, "end": v(-102.02, 58.25) * mm});
            skLineSegment(sketch, "E330", {"start": v(37.5, -35.76) * mm, "end": v(37.5, -31.16) * mm});
            skLineSegment(sketch, "E331", {"start": v(-167.4, 44.97) * mm, "end": v(-167.4, 40.37) * mm});
            skLineSegment(sketch, "E332", {"start": v(108.81, 44.95) * mm, "end": v(107.27, 40.36) * mm});
            skLineSegment(sketch, "E333", {"start": v(144.98, -53.65) * mm, "end": v(168.54, -53.65) * mm});
            skLineSegment(sketch, "E334", {"start": v(168.54, -44.44) * mm, "end": v(144.98, -44.44) * mm});
            skLineSegment(sketch, "E335", {"start": v(168.02, 35.77) * mm, "end": v(168.02, 40.36) * mm});
            skLineSegment(sketch, "E336", {"start": v(-134.2, -44.44) * mm, "end": v(-166.9, -44.44) * mm});
            skLineSegment(sketch, "E337", {"start": v(144.98, -44.44) * mm, "end": v(121.42, -44.44) * mm});
            skLineSegment(sketch, "E338", {"start": v(-102.02, 40.37) * mm, "end": v(-102.02, 44.97) * mm});
            skLineSegment(sketch, "E339", {"start": v(-134.46, -35.76) * mm, "end": v(-148.62, -35.76) * mm});
            skLineSegment(sketch, "E340", {"start": v(121.42, -44.44) * mm, "end": v(121.42, -49.05) * mm});
            skLineSegment(sketch, "E341", {"start": v(-102.02, 44.97) * mm, "end": v(-134.71, 44.97) * mm});
            skLineSegment(sketch, "E342", {"start": v(168.02, 44.95) * mm, "end": v(138.42, 44.95) * mm});
            skLineSegment(sketch, "E343", {"start": v(149.74, -31.16) * mm, "end": v(149.74, -26.56) * mm});
            skLineSegment(sketch, "E344", {"start": v(-166.9, -71.53) * mm, "end": v(-134.2, -71.53) * mm});
            skLineSegment(sketch, "E345", {"start": v(-134.71, 44.97) * mm, "end": v(-167.4, 44.97) * mm});
            skLineSegment(sketch, "E346", {"start": v(-101.5, -62.34) * mm, "end": v(-134.2, -62.34) * mm});
            skLineSegment(sketch, "E347", {"start": v(121.42, -26.56) * mm, "end": v(121.42, -31.16) * mm});
            skLineSegment(sketch, "E348", {"start": v(168.02, 40.36) * mm, "end": v(168.02, 44.95) * mm});
            skLineSegment(sketch, "E349", {"start": v(107.27, 40.36) * mm, "end": v(105.72, 35.77) * mm});
            skLineSegment(sketch, "E350", {"start": v(-101.5, -49.05) * mm, "end": v(-101.5, -44.44) * mm});
            skLineSegment(sketch, "E351", {"start": v(-101.5, -44.44) * mm, "end": v(-134.2, -44.44) * mm});
            skLineSegment(sketch, "E352", {"start": v(121.42, -31.16) * mm, "end": v(121.42, -35.76) * mm});
            skLineSegment(sketch, "E353", {"start": v(-120.3, -26.56) * mm, "end": v(-120.3, -31.16) * mm});
            skLineSegment(sketch, "E354", {"start": v(-102.02, 35.77) * mm, "end": v(-102.02, 40.37) * mm});
            skLineSegment(sketch, "E355", {"start": v(112.16, 53.65) * mm, "end": v(113.83, 58.25) * mm});
            skLineSegment(sketch, "E356", {"start": v(-120.3, -35.76) * mm, "end": v(-134.46, -35.76) * mm});
            skLineSegment(sketch, "E357", {"start": v(51.66, -26.56) * mm, "end": v(65.82, -26.56) * mm});
            skLineSegment(sketch, "E358", {"start": v(65.82, -26.56) * mm, "end": v(65.82, -31.16) * mm});
            skLineSegment(sketch, "E359", {"start": v(65.82, -31.16) * mm, "end": v(65.82, -35.76) * mm});
            skLineSegment(sketch, "E360", {"start": v(-120.3, -31.16) * mm, "end": v(-120.3, -35.76) * mm});
            skLineSegment(sketch, "E361", {"start": v(149.74, -35.76) * mm, "end": v(149.74, -31.16) * mm});
            skLineSegment(sketch, "E362", {"start": v(-101.5, -66.93) * mm, "end": v(-101.5, -62.34) * mm});
            skLineSegment(sketch, "E363", {"start": v(-134.2, -62.34) * mm, "end": v(-166.9, -62.34) * mm});
            skLineSegment(sketch, "E364", {"start": v(-166.9, -62.34) * mm, "end": v(-166.9, -66.93) * mm});
            skLineSegment(sketch, "E365", {"start": v(113.83, 58.25) * mm, "end": v(115.5, 62.85) * mm});
            skLineSegment(sketch, "E366", {"start": v(-166.9, -66.93) * mm, "end": v(-166.9, -71.53) * mm});
            skLineSegment(sketch, "E367", {"start": v(-134.2, -71.53) * mm, "end": v(-101.5, -71.53) * mm});
            skLineSegment(sketch, "E368", {"start": v(-101.5, -71.53) * mm, "end": v(-101.5, -66.93) * mm});
            skLineSegment(sketch, "E369", {"start": v(-134.46, -26.56) * mm, "end": v(-120.3, -26.56) * mm});
            skLineSegment(sketch, "E370", {"start": v(65.82, -35.76) * mm, "end": v(51.66, -35.76) * mm});
            skLineSegment(sketch, "E371", {"start": v(51.66, -35.76) * mm, "end": v(37.5, -35.76) * mm});
            skLineSegment(sketch, "E372", {"start": v(37.5, -31.16) * mm, "end": v(37.5, -26.56) * mm});
            skLineSegment(sketch, "E373", {"start": v(-148.62, -26.56) * mm, "end": v(-134.46, -26.56) * mm});
            skLineSegment(sketch, "E374", {"start": v(-148.62, -35.76) * mm, "end": v(-148.62, -31.16) * mm});
            skLineSegment(sketch, "E375", {"start": v(168.54, -53.65) * mm, "end": v(168.54, -49.05) * mm});
            skLineSegment(sketch, "E376", {"start": v(168.54, -49.05) * mm, "end": v(168.54, -44.44) * mm});
            skLineSegment(sketch, "E377", {"start": v(-101.5, -53.65) * mm, "end": v(-101.5, -49.05) * mm});
            skLineSegment(sketch, "E378", {"start": v(-134.2, -53.65) * mm, "end": v(-101.5, -53.65) * mm});
            skLineSegment(sketch, "E379", {"start": v(149.74, -26.56) * mm, "end": v(135.58, -26.56) * mm});
            skLineSegment(sketch, "E380", {"start": v(-167.4, 35.77) * mm, "end": v(-134.71, 35.77) * mm});
            skLineSegment(sketch, "E381", {"start": v(136.87, 35.77) * mm, "end": v(168.02, 35.77) * mm});
            skLineSegment(sketch, "E382", {"start": v(-166.9, -44.44) * mm, "end": v(-166.9, -49.05) * mm});
            skLineSegment(sketch, "E383", {"start": v(37.5, -26.56) * mm, "end": v(51.66, -26.56) * mm});
            skLineSegment(sketch, "E384", {"start": v(135.58, -26.56) * mm, "end": v(121.42, -26.56) * mm});
            skLineSegment(sketch, "E385", {"start": v(138.42, 44.95) * mm, "end": v(108.81, 44.95) * mm});
            skLineSegment(sketch, "E386", {"start": v(-148.62, -31.16) * mm, "end": v(-148.62, -26.56) * mm});
            skLineSegment(sketch, "E387", {"start": v(135.58, -35.76) * mm, "end": v(149.74, -35.76) * mm});
            skLineSegment(sketch, "E388", {"start": v(105.72, 35.77) * mm, "end": v(136.87, 35.77) * mm});
            skLineSegment(sketch, "E389", {"start": v(-167.4, 40.37) * mm, "end": v(-167.4, 35.77) * mm});
            skLineSegment(sketch, "E390", {"start": v(121.42, -35.76) * mm, "end": v(135.58, -35.76) * mm});
            skLineSegment(sketch, "E391", {"start": v(-166.9, -49.05) * mm, "end": v(-166.9, -53.65) * mm});
            skLineSegment(sketch, "E392", {"start": v(-166.9, -53.65) * mm, "end": v(-134.2, -53.65) * mm});
            skLineSegment(sketch, "E393", {"start": v(-134.71, 35.77) * mm, "end": v(-102.02, 35.77) * mm});
            skLineSegment(sketch, "E394", {"start": v(121.42, -53.65) * mm, "end": v(144.98, -53.65) * mm});
            skLineSegment(sketch, "E395", {"start": v(121.42, -49.05) * mm, "end": v(121.42, -53.65) * mm});
            skLineSegment(sketch, "E396", {"start": v(-187.36, -129.35) * mm, "end": v(-187.36, -97.96) * mm, "construction": true});
            skLineSegment(sketch, "E397", {"start": v(-197.82, -112.96) * mm, "end": v(-172.2, -112.96) * mm, "construction": true});
            skCircle(sketch, "E398", {"center": v(-36.4, 108.88) * mm, "radius": 1.5 * mm});
            skCircle(sketch, "E399.0.1.0", {"center": v(-187.36, -6.96) * mm, "radius": 1.5 * mm});
            skCircle(sketch, "E399.0.2.0", {"center": v(-187.36, -112.96) * mm, "radius": 1.5 * mm});
            skCircle(sketch, "E400.1.0.0", {"center": v(-0.36, -112.96) * mm, "radius": 1.5 * mm});
            skCircle(sketch, "E400.2.0.0", {"center": v(186.64, -112.96) * mm, "radius": 1.5 * mm});
            skCircle(sketch, "E401.0.1.0", {"center": v(186.64, -3.96) * mm, "radius": 1.5 * mm});
            skCircle(sketch, "E402.1.0.0", {"center": v(170.6, 108.88) * mm, "radius": 1.5 * mm});
            skSolve(sketch);
        }
        {
            var Q0;
            Q0=qSketchRegion(id+"F0",true);
            extrude(context, id + "F1", {"entities" : qUnion([Q0]), "depth" : 3 * mm});
        }
    });
